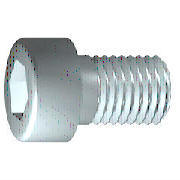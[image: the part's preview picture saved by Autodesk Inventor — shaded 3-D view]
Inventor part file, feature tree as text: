
AUTODESK INVENTOR PART (.ipt)
format: ipt  version: 2024.1 (Build 281209000, 209)  size: 186,368 bytes
history: native  units: mm (DEFAULTED — no unit token found)
features: extrude x1, plane x1, fillet x1
ambient origin geometry x7: Origin, YZ Plane, XY Plane, X Axis, Y Axis, Z Axis, Center Point
bodies: Solid1 (feature_tree), Body (feature_tree)
feature tree (3):
  extrude  "Slot"  Depth=18.0mm
  plane  "Work Plane1"
  fillet  "Fillet2"  Radius=0.306825mm
